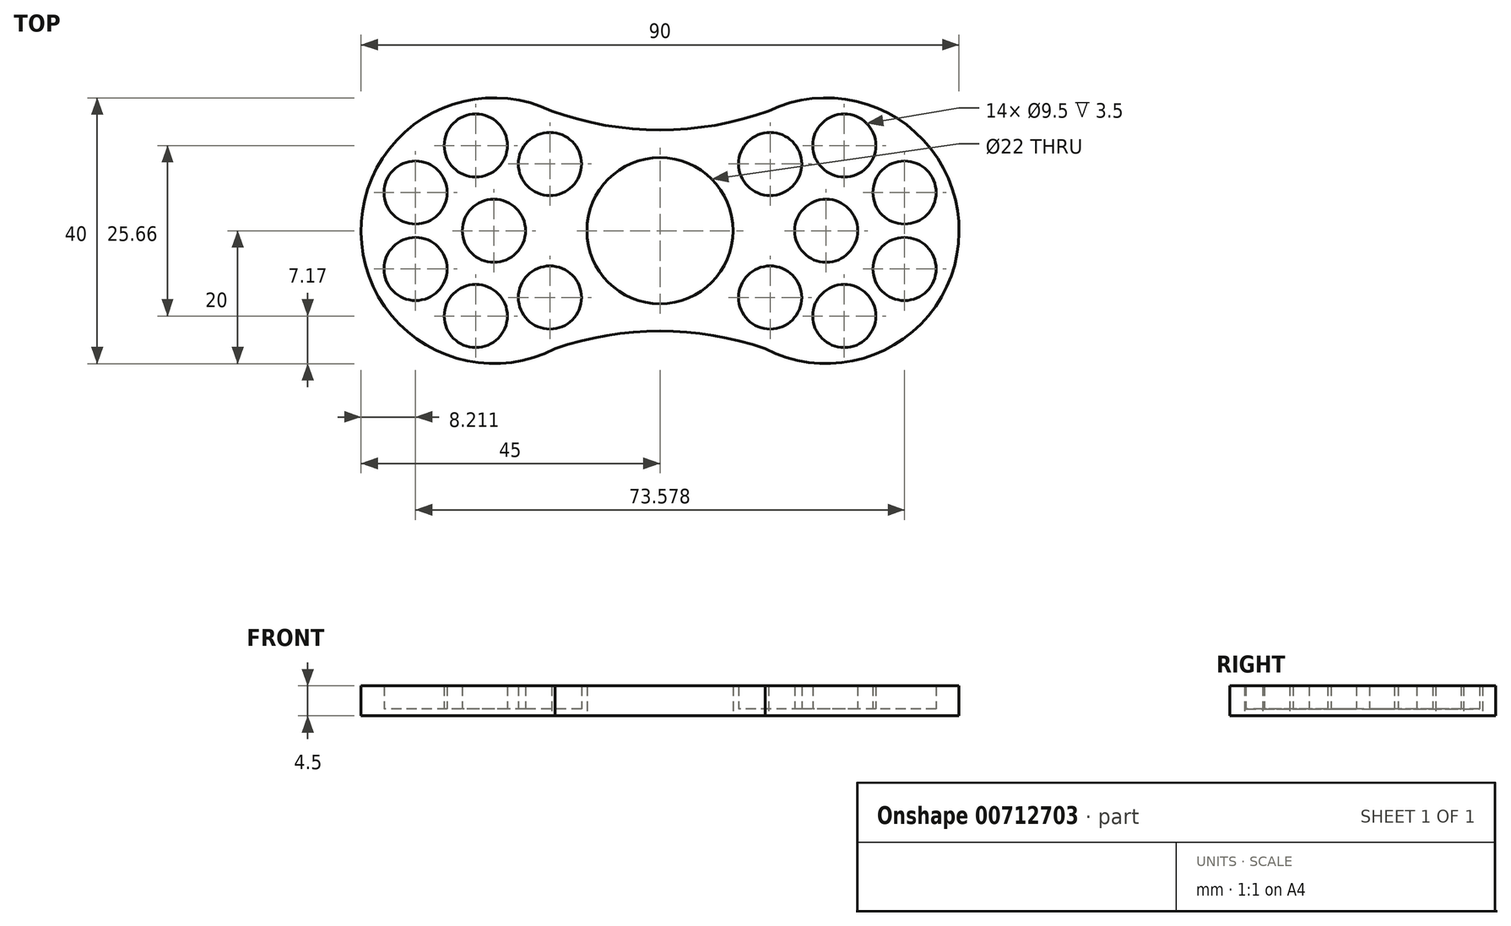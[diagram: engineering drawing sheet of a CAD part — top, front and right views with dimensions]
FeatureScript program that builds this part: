
annotation { "Feature Type Name" : "Feature", "Feature Type Description" : "" }
export const myFeature = defineFeature(function(context is Context, id is Id, definition is map)
    precondition{}
    {
        {
            var Q0;
            Q0=qCreatedBy(makeId("Top.planeOp"),FACE);
            var sketch = newSketch(context, id + "F0", { "sketchPlane" : qUnion([Q0])});
            skCircle(sketch, "E0", {"center": v(0, 0) * mm, "radius": 11 * mm});
            skPoint(sketch, "E1.center", {"position": v(-25, 0) * mm});
            skCircle(sketch, "E2", {"center": v(-25, 0) * mm, "radius": 4.75 * mm});
            skCircle(sketch, "E3", {"center": v(25, 0) * mm, "radius": 4.75 * mm});
            skArc(sketch, "E4.converted", {"start": v(15.82, -17.77) * mm, "mid": v(45, -0.28) * mm, "end": v(16.32, 18.02) * mm});
            skArc(sketch, "E5.converted", {"start": v(-16.32, 18.02) * mm, "mid": v(-45, -0.28) * mm, "end": v(-15.82, -17.77) * mm});
            skArc(sketch, "E6", {"start": v(-16.32, 18.02) * mm, "mid": v(0, 15.16) * mm, "end": v(16.32, 18.02) * mm});
            skArc(sketch, "E7", {"start": v(15.82, -17.77) * mm, "mid": v(0, -15.09) * mm, "end": v(-15.82, -17.77) * mm});
            skCircle(sketch, "E8", {"center": v(-16.57, 10.05) * mm, "radius": 4.75 * mm});
            skCircle(sketch, "E9.1.0", {"center": v(-27.73, 12.83) * mm, "radius": 4.75 * mm});
            skCircle(sketch, "E9.2.0", {"center": v(-36.79, 5.75) * mm, "radius": 4.75 * mm});
            skCircle(sketch, "E9.3.0", {"center": v(-36.79, -5.75) * mm, "radius": 4.75 * mm});
            skCircle(sketch, "E9.4.0", {"center": v(-27.73, -12.83) * mm, "radius": 4.75 * mm});
            skCircle(sketch, "E9.5.0", {"center": v(-16.57, -10.05) * mm, "radius": 4.75 * mm});
            skCircle(sketch, "E10", {"center": v(16.57, 10.05) * mm, "radius": 4.75 * mm});
            skCircle(sketch, "E11.1.0", {"center": v(27.73, 12.83) * mm, "radius": 4.75 * mm});
            skCircle(sketch, "E11.2.0", {"center": v(36.79, 5.75) * mm, "radius": 4.75 * mm});
            skCircle(sketch, "E11.3.0", {"center": v(36.79, -5.75) * mm, "radius": 4.75 * mm});
            skCircle(sketch, "E11.4.0", {"center": v(27.73, -12.83) * mm, "radius": 4.75 * mm});
            skCircle(sketch, "E11.5.0", {"center": v(16.57, -10.05) * mm, "radius": 4.75 * mm});
            skLineSegment(sketch, "E12", {"start": v(0, 0) * mm, "end": v(-25, 0) * mm});
            skLineSegment(sketch, "E13", {"start": v(-16.57, 10.05) * mm, "end": v(-25, 0) * mm});
            skLineSegment(sketch, "E14", {"start": v(-25, 0) * mm, "end": v(-16.57, -10.05) * mm});
            skSolve(sketch);
        }
        {
            var Q0;
            Q0=makeQuery(id+"F0.imprint","IMPRINT",FACE,{"disambiguationData":[TD([[makeQuery(id+"F0.imprint","IMPRINT",EDGE,{"derivedFrom":sQuery(id+"F0.wireOp",EDGE,"E0")}),-1.0]])]});
            extrude(context, id + "F1", {"entities" : qUnion([Q0]), "depth" : 4.5 * mm, "offsetDistance" : 25 * mm});
        }
        {
            var Q0;
            Q0=makeQuery(id+"F0.imprint","IMPRINT",FACE,{"disambiguationData":[TD([[makeQuery(id+"F0.imprint","IMPRINT",EDGE,{"derivedFrom":sQuery(id+"F0.wireOp",EDGE,"4e1df6f6-e819-44f6-af3a-2e676c85ef9f.5.0")}),1.0]])]});
            var Q1;
            Q1=makeQuery(id+"F0.imprint","IMPRINT",FACE,{"disambiguationData":[TD([[makeQuery(id+"F0.imprint","IMPRINT",EDGE,{"derivedFrom":sQuery(id+"F0.wireOp",EDGE,"cZsZBCqV-I1pd-xoeP-Bse6-bLMjFn0RR5nI")}),1.0]])]});
            var Q2;
            Q2=makeQuery(id+"F0.imprint","IMPRINT",FACE,{"disambiguationData":[TD([[makeQuery(id+"F0.imprint","IMPRINT",EDGE,{"derivedFrom":sQuery(id+"F0.wireOp",EDGE,"4e1df6f6-e819-44f6-af3a-2e676c85ef9f.1.0")}),1.0]])]});
            var Q3;
            Q3=makeQuery(id+"F0.imprint","IMPRINT",FACE,{"disambiguationData":[TD([[makeQuery(id+"F0.imprint","IMPRINT",EDGE,{"derivedFrom":sQuery(id+"F0.wireOp",EDGE,"E2")}),1.0]])]});
            var Q4;
            Q4=makeQuery(id+"F0.imprint","IMPRINT",FACE,{"disambiguationData":[TD([[makeQuery(id+"F0.imprint","IMPRINT",EDGE,{"derivedFrom":sQuery(id+"F0.wireOp",EDGE,"4e1df6f6-e819-44f6-af3a-2e676c85ef9f.2.0")}),1.0]])]});
            var Q5;
            Q5=makeQuery(id+"F0.imprint","IMPRINT",FACE,{"disambiguationData":[TD([[makeQuery(id+"F0.imprint","IMPRINT",EDGE,{"derivedFrom":sQuery(id+"F0.wireOp",EDGE,"4e1df6f6-e819-44f6-af3a-2e676c85ef9f.3.0")}),1.0]])]});
            var Q6;
            Q6=makeQuery(id+"F0.imprint","IMPRINT",FACE,{"disambiguationData":[TD([[makeQuery(id+"F0.imprint","IMPRINT",EDGE,{"derivedFrom":sQuery(id+"F0.wireOp",EDGE,"4e1df6f6-e819-44f6-af3a-2e676c85ef9f.4.0")}),1.0]])]});
            var Q7;
            Q7=makeQuery(id+"F0.imprint","IMPRINT",FACE,{"disambiguationData":[TD([[makeQuery(id+"F0.imprint","IMPRINT",EDGE,{"derivedFrom":sQuery(id+"F0.wireOp",EDGE,"a3476362-ac5d-48c3-ac15-c6348dd78447.2.0")}),1.0]])]});
            var Q8;
            Q8=makeQuery(id+"F0.imprint","IMPRINT",FACE,{"disambiguationData":[TD([[makeQuery(id+"F0.imprint","IMPRINT",EDGE,{"derivedFrom":sQuery(id+"F0.wireOp",EDGE,"a3476362-ac5d-48c3-ac15-c6348dd78447.3.0")}),1.0]])]});
            var Q9;
            Q9=makeQuery(id+"F0.imprint","IMPRINT",FACE,{"disambiguationData":[TD([[makeQuery(id+"F0.imprint","IMPRINT",EDGE,{"derivedFrom":sQuery(id+"F0.wireOp",EDGE,"a3476362-ac5d-48c3-ac15-c6348dd78447.4.0")}),1.0]])]});
            var Q10;
            Q10=makeQuery(id+"F0.imprint","IMPRINT",FACE,{"disambiguationData":[TD([[makeQuery(id+"F0.imprint","IMPRINT",EDGE,{"derivedFrom":sQuery(id+"F0.wireOp",EDGE,"a3476362-ac5d-48c3-ac15-c6348dd78447.5.0")}),1.0]])]});
            var Q11;
            Q11=makeQuery(id+"F0.imprint","IMPRINT",FACE,{"disambiguationData":[TD([[makeQuery(id+"F0.imprint","IMPRINT",EDGE,{"derivedFrom":sQuery(id+"F0.wireOp",EDGE,"2CHyXEpP-o0Zd-GH8N-tCiF-7Rsv5rfd8QEF")}),1.0]])]});
            var Q12;
            Q12=makeQuery(id+"F0.imprint","IMPRINT",FACE,{"disambiguationData":[TD([[makeQuery(id+"F0.imprint","IMPRINT",EDGE,{"derivedFrom":sQuery(id+"F0.wireOp",EDGE,"a3476362-ac5d-48c3-ac15-c6348dd78447.1.0")}),1.0]])]});
            var Q13;
            Q13=makeQuery(id+"F0.imprint","IMPRINT",FACE,{"disambiguationData":[TD([[makeQuery(id+"F0.imprint","IMPRINT",EDGE,{"derivedFrom":sQuery(id+"F0.wireOp",EDGE,"4c46bda0-9f7e-4fa0-8a20-7f1ee8c03dad.4.0")}),1.0]])]});
            var Q14;
            Q14=makeQuery(id+"F0.imprint","IMPRINT",FACE,{"disambiguationData":[TD([[makeQuery(id+"F0.imprint","IMPRINT",EDGE,{"derivedFrom":sQuery(id+"F0.wireOp",EDGE,"4c46bda0-9f7e-4fa0-8a20-7f1ee8c03dad.5.0")}),1.0]])]});
            var Q15;
            Q15=makeQuery(id+"F0.imprint","IMPRINT",FACE,{"disambiguationData":[TD([[makeQuery(id+"F0.imprint","IMPRINT",EDGE,{"derivedFrom":sQuery(id+"F0.wireOp",EDGE,"4c46bda0-9f7e-4fa0-8a20-7f1ee8c03dad.3.0")}),1.0]])]});
            var Q16;
            Q16=makeQuery(id+"F0.imprint","IMPRINT",FACE,{"disambiguationData":[TD([[makeQuery(id+"F0.imprint","IMPRINT",EDGE,{"derivedFrom":sQuery(id+"F0.wireOp",EDGE,"4c46bda0-9f7e-4fa0-8a20-7f1ee8c03dad.2.0")}),1.0]])]});
            var Q17;
            Q17=makeQuery(id+"F0.imprint","IMPRINT",FACE,{"disambiguationData":[TD([[makeQuery(id+"F0.imprint","IMPRINT",EDGE,{"derivedFrom":sQuery(id+"F0.wireOp",EDGE,"4c46bda0-9f7e-4fa0-8a20-7f1ee8c03dad.1.0")}),1.0]])]});
            var Q18;
            Q18=makeQuery(id+"F0.imprint","IMPRINT",FACE,{"disambiguationData":[TD([[makeQuery(id+"F0.imprint","IMPRINT",EDGE,{"derivedFrom":sQuery(id+"F0.wireOp",EDGE,"XCqX1WRV-f8Rd-YJQW-DoSE-vuXeSPOKY4FF")}),1.0]])]});
            var Q19;
            Q19=makeQuery(id+"F0.imprint","IMPRINT",FACE,{"disambiguationData":[TD([[makeQuery(id+"F0.imprint","IMPRINT",EDGE,{"derivedFrom":sQuery(id+"F0.wireOp",EDGE,"44d366ba-ee16-499c-b8f7-130e9abb6c3f.5.0")}),1.0]])]});
            var Q20;
            Q20=makeQuery(id+"F0.imprint","IMPRINT",FACE,{"disambiguationData":[TD([[makeQuery(id+"F0.imprint","IMPRINT",EDGE,{"derivedFrom":sQuery(id+"F0.wireOp",EDGE,"44d366ba-ee16-499c-b8f7-130e9abb6c3f.4.0")}),1.0]])]});
            var Q21;
            Q21=makeQuery(id+"F0.imprint","IMPRINT",FACE,{"disambiguationData":[TD([[makeQuery(id+"F0.imprint","IMPRINT",EDGE,{"derivedFrom":sQuery(id+"F0.wireOp",EDGE,"44d366ba-ee16-499c-b8f7-130e9abb6c3f.3.0")}),1.0]])]});
            var Q22;
            Q22=makeQuery(id+"F0.imprint","IMPRINT",FACE,{"disambiguationData":[TD([[makeQuery(id+"F0.imprint","IMPRINT",EDGE,{"derivedFrom":sQuery(id+"F0.wireOp",EDGE,"44d366ba-ee16-499c-b8f7-130e9abb6c3f.2.0")}),1.0]])]});
            var Q23;
            Q23=makeQuery(id+"F0.imprint","IMPRINT",FACE,{"disambiguationData":[TD([[makeQuery(id+"F0.imprint","IMPRINT",EDGE,{"derivedFrom":sQuery(id+"F0.wireOp",EDGE,"44d366ba-ee16-499c-b8f7-130e9abb6c3f.1.0")}),1.0]])]});
            var Q24;
            Q24=makeQuery(id+"F0.imprint","IMPRINT",FACE,{"disambiguationData":[TD([[makeQuery(id+"F0.imprint","IMPRINT",EDGE,{"derivedFrom":sQuery(id+"F0.wireOp",EDGE,"k0PYirwU-Hx2L-nOe0-gXHO-UjKAI2IcQulI")}),1.0]])]});
            var Q25;
            Q25=makeQuery(id+"F0.imprint","IMPRINT",FACE,{"disambiguationData":[TD([[makeQuery(id+"F0.imprint","IMPRINT",EDGE,{"derivedFrom":sQuery(id+"F0.wireOp",EDGE,"E3")}),1.0]])]});
            var Q26;
            Q26=makeQuery(id+"F0.imprint","IMPRINT",FACE,{"disambiguationData":[TD([[makeQuery(id+"F0.imprint","IMPRINT",EDGE,{"derivedFrom":sQuery(id+"F0.wireOp",EDGE,"E8")}),1.0]])]});
            var Q27;
            Q27=makeQuery(id+"F0.imprint","IMPRINT",FACE,{"disambiguationData":[TD([[makeQuery(id+"F0.imprint","IMPRINT",EDGE,{"derivedFrom":sQuery(id+"F0.wireOp",EDGE,"E9.1.0")}),1.0]])]});
            var Q28;
            Q28=makeQuery(id+"F0.imprint","IMPRINT",FACE,{"disambiguationData":[TD([[makeQuery(id+"F0.imprint","IMPRINT",EDGE,{"derivedFrom":sQuery(id+"F0.wireOp",EDGE,"E9.2.0")}),1.0]])]});
            var Q29;
            Q29=makeQuery(id+"F0.imprint","IMPRINT",FACE,{"disambiguationData":[TD([[makeQuery(id+"F0.imprint","IMPRINT",EDGE,{"derivedFrom":sQuery(id+"F0.wireOp",EDGE,"E9.3.0")}),1.0]])]});
            var Q30;
            Q30=makeQuery(id+"F0.imprint","IMPRINT",FACE,{"disambiguationData":[TD([[makeQuery(id+"F0.imprint","IMPRINT",EDGE,{"derivedFrom":sQuery(id+"F0.wireOp",EDGE,"E9.4.0")}),1.0]])]});
            var Q31;
            Q31=makeQuery(id+"F0.imprint","IMPRINT",FACE,{"disambiguationData":[TD([[makeQuery(id+"F0.imprint","IMPRINT",EDGE,{"derivedFrom":sQuery(id+"F0.wireOp",EDGE,"E9.5.0")}),1.0]])]});
            var Q32;
            Q32=makeQuery(id+"F0.imprint","IMPRINT",FACE,{"disambiguationData":[TD([[makeQuery(id+"F0.imprint","IMPRINT",EDGE,{"derivedFrom":sQuery(id+"F0.wireOp",EDGE,"E10")}),1.0]])]});
            var Q33;
            Q33=makeQuery(id+"F0.imprint","IMPRINT",FACE,{"disambiguationData":[TD([[makeQuery(id+"F0.imprint","IMPRINT",EDGE,{"derivedFrom":sQuery(id+"F0.wireOp",EDGE,"E11.1.0")}),1.0]])]});
            var Q34;
            Q34=makeQuery(id+"F0.imprint","IMPRINT",FACE,{"disambiguationData":[TD([[makeQuery(id+"F0.imprint","IMPRINT",EDGE,{"derivedFrom":sQuery(id+"F0.wireOp",EDGE,"E11.2.0")}),1.0]])]});
            var Q35;
            Q35=makeQuery(id+"F0.imprint","IMPRINT",FACE,{"disambiguationData":[TD([[makeQuery(id+"F0.imprint","IMPRINT",EDGE,{"derivedFrom":sQuery(id+"F0.wireOp",EDGE,"E11.3.0")}),1.0]])]});
            var Q36;
            Q36=makeQuery(id+"F0.imprint","IMPRINT",FACE,{"disambiguationData":[TD([[makeQuery(id+"F0.imprint","IMPRINT",EDGE,{"derivedFrom":sQuery(id+"F0.wireOp",EDGE,"E11.4.0")}),1.0]])]});
            var Q37;
            Q37=makeQuery(id+"F0.imprint","IMPRINT",FACE,{"disambiguationData":[TD([[makeQuery(id+"F0.imprint","IMPRINT",EDGE,{"derivedFrom":sQuery(id+"F0.wireOp",EDGE,"E11.5.0")}),1.0]])]});
            extrude(context, id + "F2", {"entities" : qUnion([Q0, Q1, Q2, Q3, Q4, Q5, Q6, Q7, Q8, Q9, Q10, Q11, Q12, Q13, Q14, Q15, Q16, Q17, Q18, Q19, Q20, Q21, Q22, Q23, Q24, Q25, Q26, Q27, Q28, Q29, Q30, Q31, Q32, Q33, Q34, Q35, Q36, Q37]), "operationType" : NewBodyOperationType.ADD, "depth" : 1 * mm, "offsetDistance" : 25 * mm});
        }
    });
